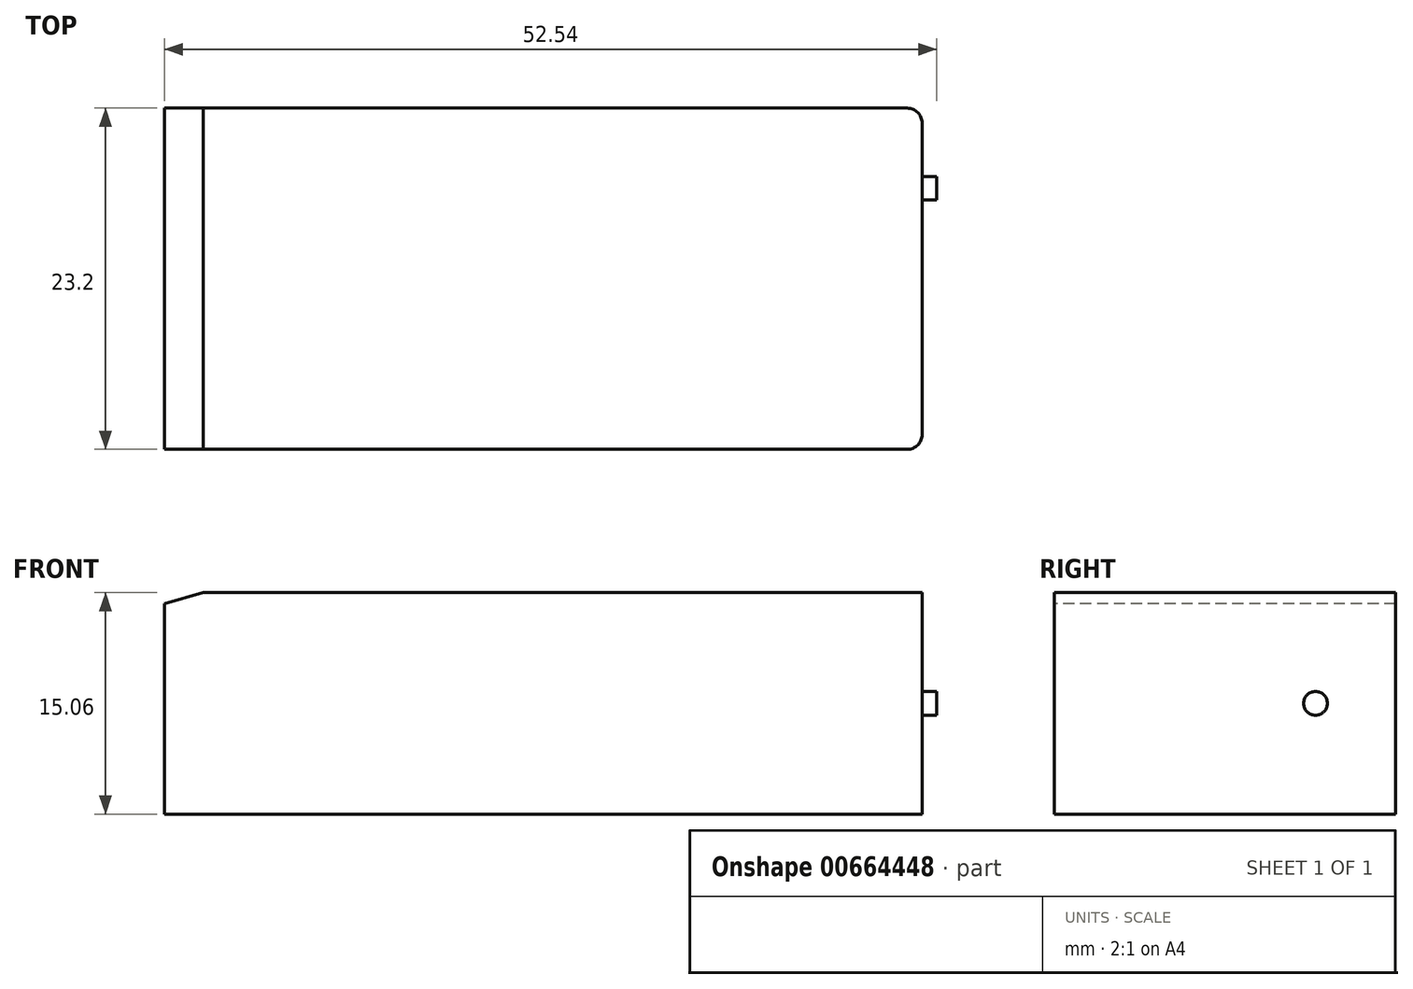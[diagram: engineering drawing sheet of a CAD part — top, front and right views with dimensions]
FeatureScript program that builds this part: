
annotation { "Feature Type Name" : "Feature", "Feature Type Description" : "" }
export const myFeature = defineFeature(function(context is Context, id is Id, definition is map)
    precondition{}
    {
        {
            var Q0;
            Q0=qCreatedBy(makeId("Top.planeOp"),FACE);
            var sketch = newSketch(context, id + "F0", { "sketchPlane" : qUnion([Q0])});
            skLineSegment(sketch, "E0.bottom", {"start": v(25.77, -11.6) * mm, "end": v(-25.77, -11.6) * mm});
            skLineSegment(sketch, "E0.top", {"start": v(25.77, 11.6) * mm, "end": v(-25.77, 11.6) * mm});
            skLineSegment(sketch, "E0.left", {"start": v(25.77, -11.6) * mm, "end": v(25.77, 11.6) * mm});
            skLineSegment(sketch, "E0.right", {"start": v(-25.77, -11.6) * mm, "end": v(-25.77, 11.6) * mm});
            skPoint(sketch, "E0.middle", {"position": v(0, 0) * mm});
            skSolve(sketch);
        }
        {
            var Q0;
            Q0=makeQuery(id+"F0.imprint","IMPRINT",FACE,{"disambiguationData":[TD([[makeQuery(id+"F0.imprint","IMPRINT",EDGE,{"derivedFrom":sQuery(id+"F0.wireOp",EDGE,"E0.bottom")}),-1.0]])]});
            extrude(context, id + "F1", {"entities" : qUnion([Q0]), "endBound" : BoundingType.SYMMETRIC, "depth" : 15.06 * mm, "offsetDistance" : 25 * mm});
        }
        {
            var Q0;
            Q0=makeQuery(id+"F1.opExtrude","SWEPT_EDGE",EDGE,{"disambiguationData":[OSD([sQuery(id+"F0.wireOp",EDGE,"E0.top"),sQuery(id+"F0.wireOp",EDGE,"E0.left")])]});
            var Q1;
            Q1=makeQuery(id+"F1.opExtrude","SWEPT_EDGE",EDGE,{"disambiguationData":[OSD([sQuery(id+"F0.wireOp",EDGE,"E0.bottom"),sQuery(id+"F0.wireOp",EDGE,"E0.left")])]});
            fillet(context, id + "F2", {"entities" : qUnion([Q0, Q1]), "radius" : 1 * mm, "tangentPropagation" : true, "allowEdgeOverflow" : false});
        }
        {
            var Q0;
            Q0=makeQuery(id+"F1.opExtrude","SWEPT_FACE",FACE,{"disambiguationData":[OSD([sQuery(id+"F0.wireOp",EDGE,"E0.left")])]});
            var sketch = newSketch(context, id + "F3", { "sketchPlane" : qUnion([Q0])});
            skCircle(sketch, "E1", {"center": v(6.15, 0) * mm, "radius": 0.8 * mm});
            skSolve(sketch);
        }
        {
            var Q0;
            Q0=makeQuery(id+"F3.imprint","IMPRINT",FACE,{"disambiguationData":[TD([[makeQuery(id+"F3.imprint","IMPRINT",EDGE,{"derivedFrom":sQuery(id+"F3.wireOp",EDGE,"E1")}),1.0]])]});
            extrude(context, id + "F4", {"entities" : qUnion([Q0]), "operationType" : NewBodyOperationType.ADD, "depth" : 1 * mm, "offsetDistance" : 25 * mm});
        }
        {
            var Q0;
            Q0=makeQuery(id+"F1.opExtrude","SWEPT_FACE",FACE,{"disambiguationData":[OSD([sQuery(id+"F0.wireOp",EDGE,"E0.bottom")])]});
            var sketch = newSketch(context, id + "F5", { "sketchPlane" : qUnion([Q0])});
            skLineSegment(sketch, "E2", {"start": v(-25.77, 6.8) * mm, "end": v(-23.1, 7.53) * mm});
            skSolve(sketch);
        }
        {
            var Q0;
            {var subQ0=sQuery(id+"F5.wireOp",EDGE,"E2");Q0=makeQuery(id+"F5.imprint","IMPRINT",FACE,{"disambiguationData":[TD([[makeQuery(id+"F5.imprint","IMPRINT",EDGE,{"derivedFrom":subQ0}),1.0]])]});}
            var Q1;
            Q1=makeQuery(id+"F1.opExtrude","SWEPT_FACE",FACE,{"disambiguationData":[OSD([sQuery(id+"F0.wireOp",EDGE,"E0.top")])]});
            extrude(context, id + "F6", {"entities" : qUnion([Q0]), "operationType" : NewBodyOperationType.REMOVE, "endBound" : BoundingType.UP_TO_SURFACE, "oppositeDirection" : true, "depth" : 25 * mm, "endBoundEntityFace" : qUnion([Q1]), "offsetDistance" : 25 * mm});
        }
    });
